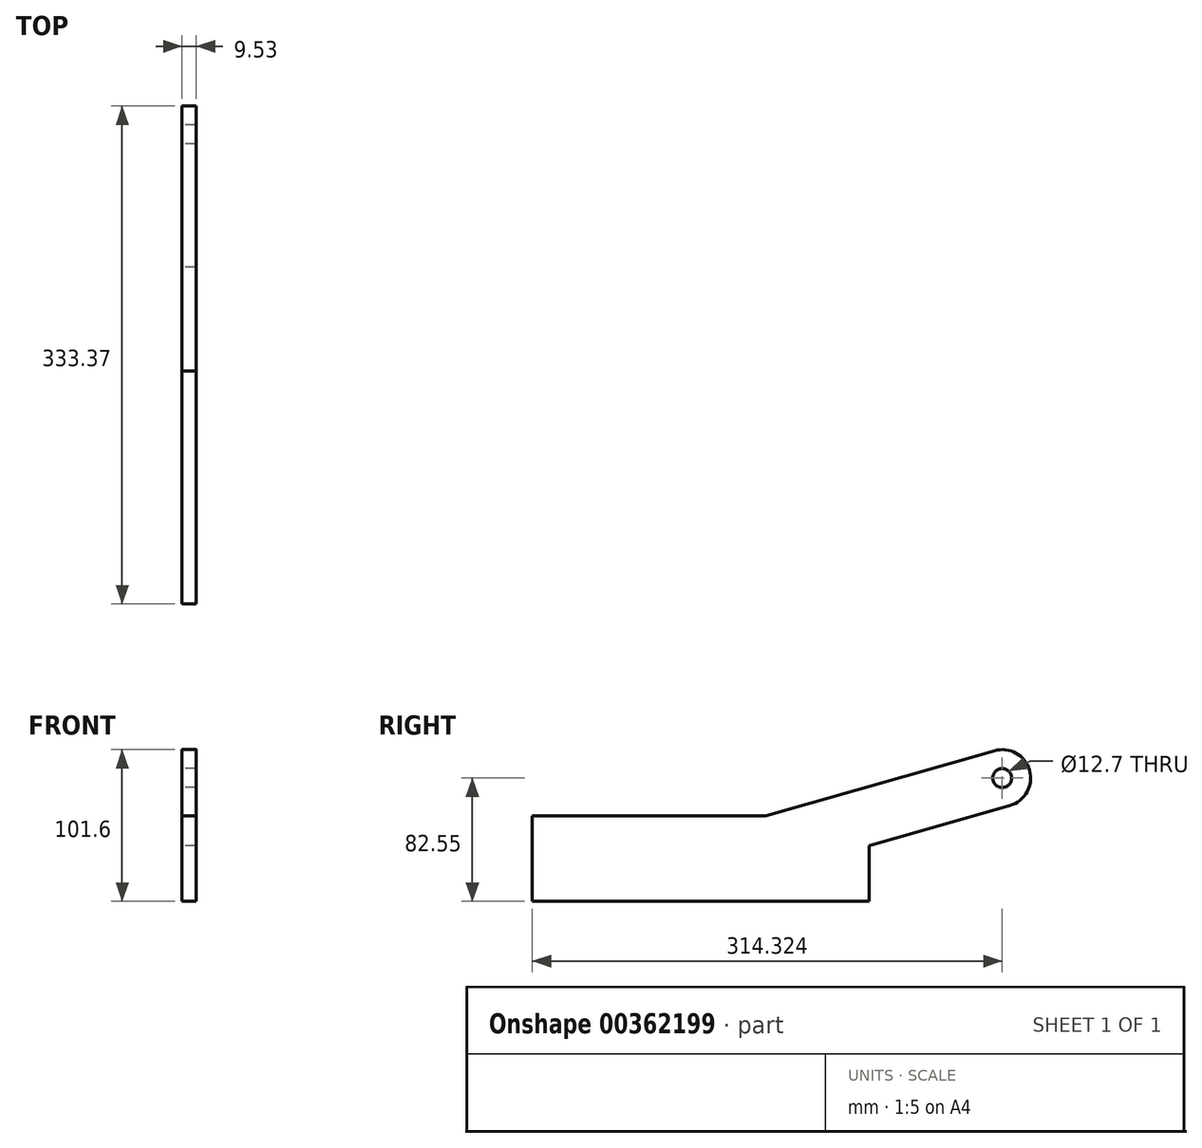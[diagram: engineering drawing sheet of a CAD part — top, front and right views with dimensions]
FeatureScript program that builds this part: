
annotation { "Feature Type Name" : "Feature", "Feature Type Description" : "" }
export const myFeature = defineFeature(function(context is Context, id is Id, definition is map)
    precondition{}
    {
        {
            var Q0;
            Q0=qCreatedBy(makeId("Right.planeOp"),FACE);
            var sketch = newSketch(context, id + "F0", { "sketchPlane" : qUnion([Q0])});
            skLineSegment(sketch, "E0.bottom", {"start": v(0, 0) * mm, "end": v(225.43, 0) * mm});
            skLineSegment(sketch, "E0.top", {"start": v(0, 57.15) * mm, "end": v(225.43, 57.15) * mm});
            skLineSegment(sketch, "E0.left", {"start": v(0, 0) * mm, "end": v(0, 57.15) * mm});
            skLineSegment(sketch, "E0.right", {"start": v(225.43, 0) * mm, "end": v(225.43, 57.15) * mm});
            skPoint(sketch, "E1", {"position": v(225.43, 57.15) * mm});
            skPoint(sketch, "E2", {"position": v(314.32, 57.15) * mm});
            skPoint(sketch, "E3", {"position": v(314.32, 82.55) * mm});
            skLineSegment(sketch, "E4", {"start": v(225.43, 57.15) * mm, "end": v(314.32, 82.55) * mm});
            skCircle(sketch, "E5", {"center": v(314.32, 82.55) * mm, "radius": 19.05 * mm});
            skLineSegment(sketch, "E6", {"start": v(314.32, 82.55) * mm, "end": v(309.1, 100.87) * mm});
            skLineSegment(sketch, "E7", {"start": v(314.32, 82.55) * mm, "end": v(319.56, 64.23) * mm});
            skLineSegment(sketch, "E8", {"start": v(319.56, 64.23) * mm, "end": v(225.43, 37.34) * mm});
            skLineSegment(sketch, "E9", {"start": v(309.1, 100.87) * mm, "end": v(156.08, 57.15) * mm});
            skSolve(sketch);
        }
        {
            var Q0;
            Q0=makeQuery(id+"F0.imprint","IMPRINT",FACE,{"disambiguationData":[TD([[makeQuery(id+"F0.imprint","IMPRINT",EDGE,{"derivedFrom":sQuery(id+"F0.wireOp",EDGE,"E0.bottom")}),1.0]])]});
            extrude(context, id + "F1", {"entities" : qUnion([Q0]), "depth" : 9.52 * mm});
        }
        {
            var Q0;
            Q0 = qSketchRegion(id + "F0", true);
            extrude(context, id + "F2", {"entities" : qUnion([Q0]), "operationType" : NewBodyOperationType.ADD, "depth" : 9.52 * mm});
        }
        {
            var Q0;
            Q0=sQuery(id+"F0.wireOp",VERTEX,"E3");
            var Q1;
            Q1=makeQuery(id+"F1.opExtrude","SWEPT_BODY",BODY,{"disambiguationData":[OSD([sQuery(id+"F0.wireOp",EDGE,"E0.bottom"),sQuery(id+"F0.wireOp",EDGE,"E0.top"),sQuery(id+"F0.wireOp",EDGE,"E0.left"),sQuery(id+"F0.wireOp",EDGE,"E0.right")])]});
            hole(context, id + "F3", {"style" : HoleStyle.SIMPLE, "endStyle" : HoleEndStyle.THROUGH, "oppositeDirection" : true, "holeDiameter" : 12.7 * mm, "isTappedThrough" : true, "tappedDepth" : 12.7 * mm, "tapClearance" : 3, "startFromSketch" : true, "locations" : qUnion([Q0]), "scope" : qUnion([Q1])});
        }
    });
